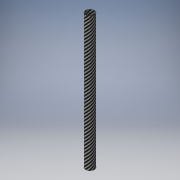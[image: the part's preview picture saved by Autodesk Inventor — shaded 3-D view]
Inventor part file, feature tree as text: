
AUTODESK INVENTOR PART (.ipt)
format: ipt  version: 2018 (Build 220112000, 112)  size: 109,568 bytes
history: native  units: in
note: dims shown in document units (in); Inventor stores cm internally (conversion verified against a paired STEP export)
features: extrude x1, sketch x1
ambient origin geometry x8: Origin, YZ Plane, XZ Plane, XY Plane, X Axis, Y Axis, Z Axis, Center Point
bodies: Solid1 (feature_tree)
feature tree (2):
  extrude  "Extrusion1"  Depth=6.4563in
  sketch  "Sketch1"  dims[d0=0.42in d1=0.39in d2=6.4563in d3=0.0in]
